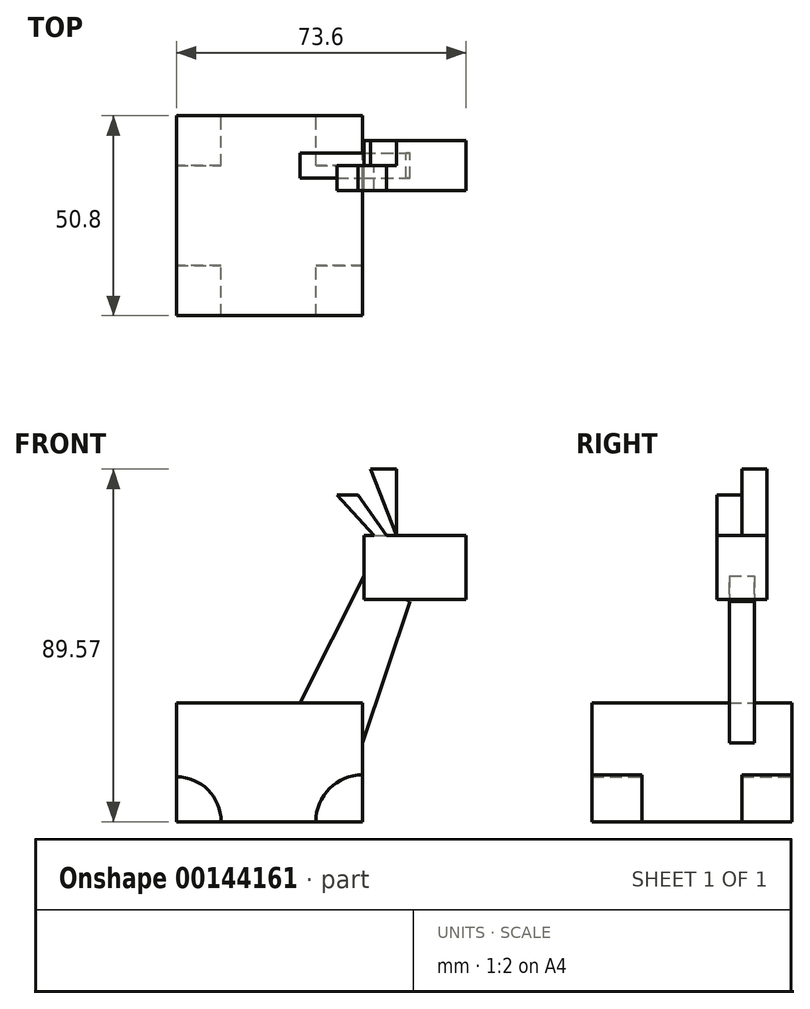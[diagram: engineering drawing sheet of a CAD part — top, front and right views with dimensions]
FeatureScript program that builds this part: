
annotation { "Feature Type Name" : "Feature", "Feature Type Description" : "" }
export const myFeature = defineFeature(function(context is Context, id is Id, definition is map)
    precondition{}
    {
        {
            var Q0;
            Q0=qCreatedBy(makeId("Front.planeOp"),FACE);
            var sketch = newSketch(context, id + "F0", { "sketchPlane" : qUnion([Q0])});
            skLineSegment(sketch, "E0.bottom", {"start": v(-31.38, -11.55) * mm, "end": v(15.97, -11.55) * mm});
            skLineSegment(sketch, "E0.top", {"start": v(-31.38, -41.79) * mm, "end": v(15.97, -41.79) * mm});
            skLineSegment(sketch, "E0.left", {"start": v(-31.38, -11.55) * mm, "end": v(-31.38, -41.79) * mm});
            skLineSegment(sketch, "E0.right", {"start": v(15.97, -11.55) * mm, "end": v(15.97, -41.79) * mm});
            skLineSegment(sketch, "E1", {"start": v(0, -11.55) * mm, "end": v(16.26, 20.68) * mm});
            skLineSegment(sketch, "E2", {"start": v(16.26, 20.68) * mm, "end": v(15.97, -21.82) * mm});
            skLineSegment(sketch, "E3", {"start": v(15.97, -21.82) * mm, "end": v(27.95, 14.12) * mm});
            skLineSegment(sketch, "E4", {"start": v(27.95, 14.12) * mm, "end": v(16.26, 20.68) * mm});
            skLineSegment(sketch, "E5.bottom", {"start": v(16.26, 30.95) * mm, "end": v(42.22, 30.95) * mm});
            skLineSegment(sketch, "E5.top", {"start": v(16.26, 14.69) * mm, "end": v(42.22, 14.69) * mm});
            skLineSegment(sketch, "E5.left", {"start": v(16.26, 30.95) * mm, "end": v(16.26, 14.69) * mm});
            skLineSegment(sketch, "E5.right", {"start": v(42.22, 30.95) * mm, "end": v(42.22, 14.69) * mm});
            skLineSegment(sketch, "E6", {"start": v(18.83, 30.95) * mm, "end": v(9.41, 41.22) * mm});
            skLineSegment(sketch, "E7", {"start": v(9.41, 41.22) * mm, "end": v(14.83, 41.22) * mm});
            skLineSegment(sketch, "E8", {"start": v(14.83, 41.22) * mm, "end": v(21.96, 30.95) * mm});
            skLineSegment(sketch, "E9", {"start": v(24.53, 30.95) * mm, "end": v(24.53, 47.78) * mm});
            skLineSegment(sketch, "E10", {"start": v(24.53, 47.78) * mm, "end": v(17.97, 47.78) * mm});
            skLineSegment(sketch, "E11", {"start": v(17.97, 47.78) * mm, "end": v(24.53, 30.95) * mm});
            skCircle(sketch, "E12", {"center": v(-31.38, -41.79) * mm, "radius": 11.4 * mm});
            skCircle(sketch, "E13", {"center": v(15.97, -41.79) * mm, "radius": 11.92 * mm});
            skSolve(sketch);
        }
        {
            var Q0;
            {var subQ0=sQuery(id+"F0.wireOp",EDGE,"E0.left");var subQ1=sQuery(id+"F0.wireOp",EDGE,"E0.bottom");var subQ2=makeQuery(id+"F0.imprint","INTERSECT",VERTEX,{"derivedFrom":[subQ1,subQ0]});Q0=makeQuery(id+"F0.imprint","IMPRINT",FACE,{"disambiguationData":[TD([[makeQuery(id+"F0.imprint","IMPRINT",EDGE,{"disambiguationData":[TD([[subQ2,-1.0]])],"derivedFrom":subQ1}),-1.0]])]});}
            extrude(context, id + "F1", {"entities" : qUnion([Q0]), "endBound" : BoundingType.SYMMETRIC, "depth" : 25.4 * mm});
        }
        {
            var Q0;
            {var subQ3=sQuery(id+"F0.wireOp",EDGE,"E1");Q0=makeQuery(id+"F0.imprint","IMPRINT",FACE,{"disambiguationData":[TD([[makeQuery(id+"F0.imprint","IMPRINT",EDGE,{"derivedFrom":subQ3}),-1.0]])]});}
            var Q1;
            {var subQ6=sQuery(id+"F0.wireOp",EDGE,"E2");Q1=makeQuery(id+"F0.imprint","IMPRINT",FACE,{"disambiguationData":[TD([[makeQuery(id+"F0.imprint","IMPRINT",EDGE,{"derivedFrom":subQ6}),1.0]])]});}
            extrude(context, id + "F2", {"entities" : qUnion([Q0, Q1]), "operationType" : NewBodyOperationType.ADD, "endBound" : BoundingType.SYMMETRIC, "depth" : 6.35 * mm});
        }
        {
            var Q0;
            {var subQ10=sQuery(id+"F0.wireOp",EDGE,"E5.right");Q0=makeQuery(id+"F0.imprint","IMPRINT",FACE,{"disambiguationData":[TD([[makeQuery(id+"F0.imprint","IMPRINT",EDGE,{"derivedFrom":subQ10}),-1.0]])]});}
            var Q1;
            {var subQ0=sQuery(id+"F0.wireOp",EDGE,"E5.left");var subQ3=sQuery(id+"F0.wireOp",EDGE,"E5.top");var subQ5=makeQuery(id+"F0.imprint","INTERSECT",VERTEX,{"derivedFrom":[subQ3,subQ0]});Q1=makeQuery(id+"F0.imprint","IMPRINT",FACE,{"disambiguationData":[TD([[makeQuery(id+"F0.imprint","IMPRINT",EDGE,{"disambiguationData":[TD([[subQ5,-1.0]])],"derivedFrom":subQ3}),1.0]])]});}
            extrude(context, id + "F3", {"entities" : qUnion([Q0, Q1]), "operationType" : NewBodyOperationType.ADD, "endBound" : BoundingType.SYMMETRIC, "depth" : 12.7 * mm});
        }
        {
            var Q0;
            {var subQ0=sQuery(id+"F0.wireOp",EDGE,"E6");Q0=makeQuery(id+"F0.imprint","IMPRINT",FACE,{"disambiguationData":[TD([[makeQuery(id+"F0.imprint","IMPRINT",EDGE,{"derivedFrom":subQ0}),-1.0]])]});}
            var Q1;
            Q1=makeQuery(id+"F3.opExtrude","CAP_FACE",FACE,{"disambiguationData":[OSD([sQuery(id+"F0.wireOp",EDGE,"E5.bottom"),sQuery(id+"F0.wireOp",EDGE,"E5.top"),sQuery(id+"F0.wireOp",EDGE,"E5.left"),sQuery(id+"F0.wireOp",EDGE,"E5.right")])],"isStart":false});
            extrude(context, id + "F4", {"entities" : qUnion([Q0]), "operationType" : NewBodyOperationType.ADD, "endBound" : BoundingType.UP_TO_SURFACE, "endBoundEntityFace" : qUnion([Q1]), "depth" : 25.4 * mm});
        }
        {
            var Q0;
            Q0=makeQuery(id+"F0.imprint","IMPRINT",FACE,{"disambiguationData":[TD([[makeQuery(id+"F0.imprint","IMPRINT",EDGE,{"derivedFrom":sQuery(id+"F0.wireOp",EDGE,"E9")}),1.0]])]});
            var Q1;
            Q1=makeQuery(id+"F3.opExtrude","CAP_FACE",FACE,{"disambiguationData":[OSD([sQuery(id+"F0.wireOp",EDGE,"E5.bottom"),sQuery(id+"F0.wireOp",EDGE,"E5.top"),sQuery(id+"F0.wireOp",EDGE,"E5.left"),sQuery(id+"F0.wireOp",EDGE,"E5.right")])],"isStart":true});
            extrude(context, id + "F5", {"entities" : qUnion([Q0]), "endBound" : BoundingType.UP_TO_SURFACE, "oppositeDirection" : true, "endBoundEntityFace" : qUnion([Q1]), "depth" : 2.54 * mm});
        }
        {
            var Q0;
            {var subQ0=sQuery(id+"F0.wireOp",EDGE,"E0.right");var subQ1=sQuery(id+"F0.wireOp",EDGE,"E0.top");var subQ2=makeQuery(id+"F0.imprint","INTERSECT",VERTEX,{"derivedFrom":[subQ1,subQ0]});Q0=makeQuery(id+"F0.imprint","IMPRINT",FACE,{"disambiguationData":[TD([[makeQuery(id+"F0.imprint","IMPRINT",EDGE,{"disambiguationData":[TD([[subQ2,1.0]])],"derivedFrom":subQ1}),1.0]])]});}
            var Q1;
            {var subQ0=sQuery(id+"F0.wireOp",EDGE,"E0.left");var subQ1=sQuery(id+"F0.wireOp",EDGE,"E0.top");var subQ2=makeQuery(id+"F0.imprint","INTERSECT",VERTEX,{"derivedFrom":[subQ1,subQ0]});Q1=makeQuery(id+"F0.imprint","IMPRINT",FACE,{"disambiguationData":[TD([[makeQuery(id+"F0.imprint","IMPRINT",EDGE,{"disambiguationData":[TD([[subQ2,-1.0]])],"derivedFrom":subQ1}),1.0]])]});}
            var Q2;
            Q2=makeQuery(id+"F1.opExtrude","CAP_FACE",FACE,{"disambiguationData":[OSD([sQuery(id+"F0.wireOp",EDGE,"E0.bottom"),sQuery(id+"F0.wireOp",EDGE,"E0.top"),sQuery(id+"F0.wireOp",EDGE,"E0.left"),sQuery(id+"F0.wireOp",EDGE,"E0.right"),sQuery(id+"F0.wireOp",EDGE,"E12"),sQuery(id+"F0.wireOp",EDGE,"E13")])],"isStart":false});
            extrude(context, id + "F6", {"entities" : qUnion([Q0, Q1, Q2]), "operationType" : NewBodyOperationType.ADD, "depth" : 25.4 * mm});
        }
    });
